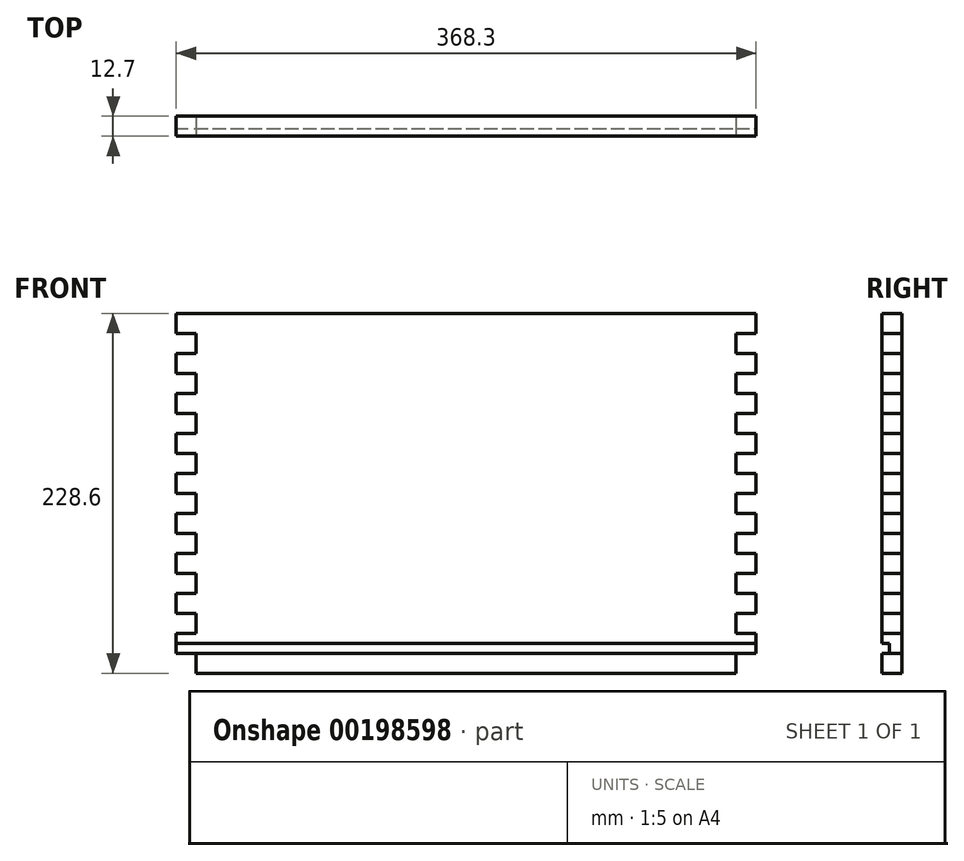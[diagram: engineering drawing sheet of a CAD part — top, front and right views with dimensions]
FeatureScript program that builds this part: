
annotation { "Feature Type Name" : "Feature", "Feature Type Description" : "" }
export const myFeature = defineFeature(function(context is Context, id is Id, definition is map)
    precondition{}
    {
        {
            var Q0;
            Q0=qCreatedBy(makeId("Front.planeOp"),FACE);
            var sketch = newSketch(context, id + "F0", { "sketchPlane" : qUnion([Q0])});
            skLineSegment(sketch, "E0.bottom", {"start": v(-184.15, 114.3) * mm, "end": v(184.15, 114.3) * mm});
            skLineSegment(sketch, "E0.top", {"start": v(-184.15, -114.3) * mm, "end": v(184.15, -114.3) * mm});
            skLineSegment(sketch, "E0.left", {"start": v(-184.15, 114.3) * mm, "end": v(-184.15, -114.3) * mm});
            skLineSegment(sketch, "E0.right", {"start": v(184.15, 114.3) * mm, "end": v(184.15, -114.3) * mm});
            skPoint(sketch, "E0.middle", {"position": v(0, 0) * mm});
            skSolve(sketch);
        }
        {
            var Q0;
            Q0 = qSketchRegion(id + "F0", true);
            extrude(context, id + "F1", {"entities" : qUnion([Q0]), "depth" : 12.7 * mm});
        }
        {
            var Q0;
            Q0=makeQuery(id+"F1.opExtrude","CAP_FACE",FACE,{"disambiguationData":[OSD([sQuery(id+"F0.wireOp",EDGE,"E0.bottom"),sQuery(id+"F0.wireOp",EDGE,"E0.top"),sQuery(id+"F0.wireOp",EDGE,"E0.left"),sQuery(id+"F0.wireOp",EDGE,"E0.right")])],"isStart":false});
            var sketch = newSketch(context, id + "F2", { "sketchPlane" : qUnion([Q0])});
            skPoint(sketch, "E1.endSnap0", {"position": v(0, 114.3) * mm});
            skLineSegment(sketch, "E2.bottom", {"start": v(-184.15, 101.6) * mm, "end": v(-171.45, 101.6) * mm});
            skLineSegment(sketch, "E2.top", {"start": v(-184.15, 88.9) * mm, "end": v(-171.45, 88.9) * mm});
            skLineSegment(sketch, "E2.left", {"start": v(-184.15, 101.6) * mm, "end": v(-184.15, 88.9) * mm});
            skLineSegment(sketch, "E2.right", {"start": v(-171.45, 101.6) * mm, "end": v(-171.45, 88.9) * mm});
            skLineSegment(sketch, "E3.0.1.0", {"start": v(-184.15, 63.5) * mm, "end": v(-171.45, 63.5) * mm});
            skLineSegment(sketch, "E3.0.1.1", {"start": v(-171.45, 76.2) * mm, "end": v(-171.45, 63.5) * mm});
            skLineSegment(sketch, "E3.0.1.2", {"start": v(-184.15, 76.2) * mm, "end": v(-184.15, 63.5) * mm});
            skLineSegment(sketch, "E3.0.1.3", {"start": v(-184.15, 76.2) * mm, "end": v(-171.45, 76.2) * mm});
            skLineSegment(sketch, "E3.0.2.0", {"start": v(-184.15, 38.1) * mm, "end": v(-171.45, 38.1) * mm});
            skLineSegment(sketch, "E3.0.2.1", {"start": v(-171.45, 50.8) * mm, "end": v(-171.45, 38.1) * mm});
            skLineSegment(sketch, "E3.0.2.2", {"start": v(-184.15, 50.8) * mm, "end": v(-184.15, 38.1) * mm});
            skLineSegment(sketch, "E3.0.2.3", {"start": v(-184.15, 50.8) * mm, "end": v(-171.45, 50.8) * mm});
            skLineSegment(sketch, "E3.0.3.0", {"start": v(-184.15, 12.7) * mm, "end": v(-171.45, 12.7) * mm});
            skLineSegment(sketch, "E3.0.3.1", {"start": v(-171.45, 25.4) * mm, "end": v(-171.45, 12.7) * mm});
            skLineSegment(sketch, "E3.0.3.2", {"start": v(-184.15, 25.4) * mm, "end": v(-184.15, 12.7) * mm});
            skLineSegment(sketch, "E3.0.3.3", {"start": v(-184.15, 25.4) * mm, "end": v(-171.45, 25.4) * mm});
            skLineSegment(sketch, "E3.0.4.0", {"start": v(-184.15, -12.7) * mm, "end": v(-171.45, -12.7) * mm});
            skLineSegment(sketch, "E3.0.4.1", {"start": v(-171.45, 0) * mm, "end": v(-171.45, -12.7) * mm});
            skLineSegment(sketch, "E3.0.4.2", {"start": v(-184.15, 0) * mm, "end": v(-184.15, -12.7) * mm});
            skLineSegment(sketch, "E3.0.4.3", {"start": v(-184.15, 0) * mm, "end": v(-171.45, 0) * mm});
            skLineSegment(sketch, "E3.0.5.0", {"start": v(-184.15, -38.1) * mm, "end": v(-171.45, -38.1) * mm});
            skLineSegment(sketch, "E3.0.5.1", {"start": v(-171.45, -25.4) * mm, "end": v(-171.45, -38.1) * mm});
            skLineSegment(sketch, "E3.0.5.2", {"start": v(-184.15, -25.4) * mm, "end": v(-184.15, -38.1) * mm});
            skLineSegment(sketch, "E3.0.5.3", {"start": v(-184.15, -25.4) * mm, "end": v(-171.45, -25.4) * mm});
            skLineSegment(sketch, "E3.0.6.0", {"start": v(-184.15, -63.5) * mm, "end": v(-171.45, -63.5) * mm});
            skLineSegment(sketch, "E3.0.6.1", {"start": v(-171.45, -50.8) * mm, "end": v(-171.45, -63.5) * mm});
            skLineSegment(sketch, "E3.0.6.2", {"start": v(-184.15, -50.8) * mm, "end": v(-184.15, -63.5) * mm});
            skLineSegment(sketch, "E3.0.6.3", {"start": v(-184.15, -50.8) * mm, "end": v(-171.45, -50.8) * mm});
            skLineSegment(sketch, "E3.0.7.0", {"start": v(-184.15, -88.9) * mm, "end": v(-171.45, -88.9) * mm});
            skLineSegment(sketch, "E3.0.7.1", {"start": v(-171.45, -76.2) * mm, "end": v(-171.45, -88.9) * mm});
            skLineSegment(sketch, "E3.0.7.2", {"start": v(-184.15, -76.2) * mm, "end": v(-184.15, -88.9) * mm});
            skLineSegment(sketch, "E3.0.7.3", {"start": v(-184.15, -76.2) * mm, "end": v(-171.45, -76.2) * mm});
            skLineSegment(sketch, "E3.0.8.0", {"start": v(-184.15, -114.3) * mm, "end": v(-171.45, -114.3) * mm});
            skLineSegment(sketch, "E3.0.8.1", {"start": v(-171.45, -101.6) * mm, "end": v(-171.45, -114.3) * mm});
            skLineSegment(sketch, "E3.0.8.2", {"start": v(-184.15, -101.6) * mm, "end": v(-184.15, -114.3) * mm});
            skLineSegment(sketch, "E3.0.8.3", {"start": v(-184.15, -101.6) * mm, "end": v(-171.45, -101.6) * mm});
            skLineSegment(sketch, "E4.MirrorCS", {"start": v(184.15, 76.2) * mm, "end": v(184.15, 63.5) * mm});
            skLineSegment(sketch, "E5.MirrorCS", {"start": v(184.15, 63.5) * mm, "end": v(171.45, 63.5) * mm});
            skLineSegment(sketch, "E6.MirrorCS", {"start": v(184.15, 101.6) * mm, "end": v(171.45, 101.6) * mm});
            skLineSegment(sketch, "E7.MirrorCS", {"start": v(184.15, 88.9) * mm, "end": v(171.45, 88.9) * mm});
            skLineSegment(sketch, "E8.MirrorCS", {"start": v(184.15, -88.9) * mm, "end": v(171.45, -88.9) * mm});
            skLineSegment(sketch, "E9.MirrorCS", {"start": v(184.15, -101.6) * mm, "end": v(184.15, -114.3) * mm});
            skLineSegment(sketch, "E10.MirrorCS", {"start": v(184.15, 101.6) * mm, "end": v(184.15, 88.9) * mm});
            skLineSegment(sketch, "E11.MirrorCS", {"start": v(184.15, -50.8) * mm, "end": v(184.15, -63.5) * mm});
            skLineSegment(sketch, "E12.MirrorCS", {"start": v(184.15, -12.7) * mm, "end": v(171.45, -12.7) * mm});
            skLineSegment(sketch, "E13.MirrorCS", {"start": v(184.15, 25.4) * mm, "end": v(171.45, 25.4) * mm});
            skLineSegment(sketch, "E14.MirrorCS", {"start": v(171.45, 76.2) * mm, "end": v(171.45, 63.5) * mm});
            skLineSegment(sketch, "E15.MirrorCS", {"start": v(184.15, -101.6) * mm, "end": v(171.45, -101.6) * mm});
            skLineSegment(sketch, "E16.MirrorCS", {"start": v(184.15, 0) * mm, "end": v(171.45, 0) * mm});
            skLineSegment(sketch, "E17.MirrorCS", {"start": v(184.15, -76.2) * mm, "end": v(171.45, -76.2) * mm});
            skLineSegment(sketch, "E18.MirrorCS", {"start": v(184.15, 50.8) * mm, "end": v(184.15, 38.1) * mm});
            skLineSegment(sketch, "E19.MirrorCS", {"start": v(184.15, -38.1) * mm, "end": v(171.45, -38.1) * mm});
            skLineSegment(sketch, "E20.MirrorCS", {"start": v(184.15, -25.4) * mm, "end": v(171.45, -25.4) * mm});
            skLineSegment(sketch, "E21.MirrorCS", {"start": v(184.15, 25.4) * mm, "end": v(184.15, 12.7) * mm});
            skLineSegment(sketch, "E22.MirrorCS", {"start": v(171.45, 50.8) * mm, "end": v(171.45, 38.1) * mm});
            skLineSegment(sketch, "E23.MirrorCS", {"start": v(184.15, -63.5) * mm, "end": v(171.45, -63.5) * mm});
            skLineSegment(sketch, "E24.MirrorCS", {"start": v(171.45, -101.6) * mm, "end": v(171.45, -114.3) * mm});
            skLineSegment(sketch, "E25.MirrorCS", {"start": v(171.45, -25.4) * mm, "end": v(171.45, -38.1) * mm});
            skLineSegment(sketch, "E26.MirrorCS", {"start": v(184.15, -50.8) * mm, "end": v(171.45, -50.8) * mm});
            skLineSegment(sketch, "E27.MirrorCS", {"start": v(171.45, 0) * mm, "end": v(171.45, -12.7) * mm});
            skLineSegment(sketch, "E28.MirrorCS", {"start": v(184.15, 0) * mm, "end": v(184.15, -12.7) * mm});
            skLineSegment(sketch, "E29.MirrorCS", {"start": v(184.15, 50.8) * mm, "end": v(171.45, 50.8) * mm});
            skLineSegment(sketch, "E30.MirrorCS", {"start": v(184.15, 38.1) * mm, "end": v(171.45, 38.1) * mm});
            skLineSegment(sketch, "E31.MirrorCS", {"start": v(184.15, -25.4) * mm, "end": v(184.15, -38.1) * mm});
            skLineSegment(sketch, "E32.MirrorCS", {"start": v(184.15, 76.2) * mm, "end": v(171.45, 76.2) * mm});
            skLineSegment(sketch, "E33.MirrorCS", {"start": v(171.45, 25.4) * mm, "end": v(171.45, 12.7) * mm});
            skLineSegment(sketch, "E34.MirrorCS", {"start": v(171.45, -76.2) * mm, "end": v(171.45, -88.9) * mm});
            skLineSegment(sketch, "E35.MirrorCS", {"start": v(184.15, 12.7) * mm, "end": v(171.45, 12.7) * mm});
            skLineSegment(sketch, "E36.MirrorCS", {"start": v(184.15, -114.3) * mm, "end": v(171.45, -114.3) * mm});
            skLineSegment(sketch, "E37.MirrorCS", {"start": v(184.15, -76.2) * mm, "end": v(184.15, -88.9) * mm});
            skLineSegment(sketch, "E38.MirrorCS", {"start": v(171.45, -50.8) * mm, "end": v(171.45, -63.5) * mm});
            skLineSegment(sketch, "E39.MirrorCS", {"start": v(171.45, 101.6) * mm, "end": v(171.45, 88.9) * mm});
            skSolve(sketch);
        }
        {
            var Q0;
            Q0 = qSketchRegion(id + "F2", true);
            extrude(context, id + "F3", {"entities" : qUnion([Q0]), "operationType" : NewBodyOperationType.REMOVE, "oppositeDirection" : true, "depth" : 25.4 * mm});
        }
        {
            var Q0;
            Q0 = qSketchRegion(id + "F2", true);
            extrude(context, id + "F4", {"entities" : qUnion([Q0]), "operationType" : NewBodyOperationType.REMOVE, "oppositeDirection" : true, "depth" : 25.4 * mm});
        }
        {
            var Q0;
            Q0=makeQuery(id+"F1.opExtrude","CAP_FACE",FACE,{"disambiguationData":[OSD([sQuery(id+"F0.wireOp",EDGE,"E0.bottom"),sQuery(id+"F0.wireOp",EDGE,"E0.top"),sQuery(id+"F0.wireOp",EDGE,"E0.left"),sQuery(id+"F0.wireOp",EDGE,"E0.right")])],"isStart":false});
            var sketch = newSketch(context, id + "F5", { "sketchPlane" : qUnion([Q0])});
            skLineSegment(sketch, "E40.bottom", {"start": v(-184.15, -101.6) * mm, "end": v(184.15, -101.6) * mm});
            skLineSegment(sketch, "E40.top", {"start": v(-184.15, -95.25) * mm, "end": v(184.15, -95.25) * mm});
            skLineSegment(sketch, "E40.left", {"start": v(-184.15, -101.6) * mm, "end": v(-184.15, -95.25) * mm});
            skLineSegment(sketch, "E40.right", {"start": v(184.15, -101.6) * mm, "end": v(184.15, -95.25) * mm});
            skSolve(sketch);
        }
        {
            var Q0;
            Q0 = qSketchRegion(id + "F5", true);
            extrude(context, id + "F6", {"entities" : qUnion([Q0]), "operationType" : NewBodyOperationType.REMOVE, "oppositeDirection" : true, "depth" : 4.76 * mm});
        }
    });
